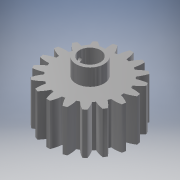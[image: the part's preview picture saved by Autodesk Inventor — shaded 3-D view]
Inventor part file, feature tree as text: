
AUTODESK INVENTOR PART (.ipt)
format: ipt  version: 2018 (Build 220112000, 112)  size: 299,520 bytes
history: native  units: mm (DEFAULTED — no unit token found)
features: sketch x5, extrude x4, plane x4, other x3, projected_geometry x2
ambient origin geometry x8: Origin, YZ Plane, XZ Plane, XY Plane, X Axis, Y Axis, Z Axis, Center Point
bodies: Body1 (feature_tree), Body2 (feature_tree)
feature tree (18):
  extrude  "Extrusion1"  Depth=30.0mm TaperAngle=0.0deg
  plane  "Work Plane2"
  plane  "Work Plane8"
  plane  "Work Plane9"
  other  "Engranaje recto"
  extrude  "Extrusión2"  Depth=10.0mm TaperAngle=0.0deg
  extrude  "Extrusión3"  Depth=1.745329mm TaperAngle=0.0deg
  plane  "Plano de trabajo11"
  extrude  "Extrusión4"  TaperAngle=0.0deg  [1 undecoded]
  sketch  "Sketch1"  dims[d0=60.0mm d1=30.0mm d2=0.0mm]
  sketch  "Sketch2"  dims[d3=54.0mm d4=10.0mm d5=0.0mm]
  other  "Srf1"
  sketch  "Boceto3"  dims[d16=108.0mm d17=0.0mm d34=1.745329mm]
  sketch  "Boceto4"  dims[d39=0.0mm d41=0.0mm]
  projected_geometry  "Contorno proyectado1"
  sketch  "Boceto5"  dims[d43=108.0mm d46=108.0mm d47=0.0mm d48=0.0mm d49=15.0mm d50=10.0mm d51=0.0mm d52=2.5mm d53=12.0mm d54=0.0mm d55=-12.75mm d56=3.0mm d57=6.2mm d58=0.0mm]
  projected_geometry  "Contorno proyectado2"
  other  "Diámetro de separación"
note: 1 required parameter value undecoded (feature->parameter linkage not recoverable at this tier; creation-order binding heuristic only, values carry confidence <= 0.55)
